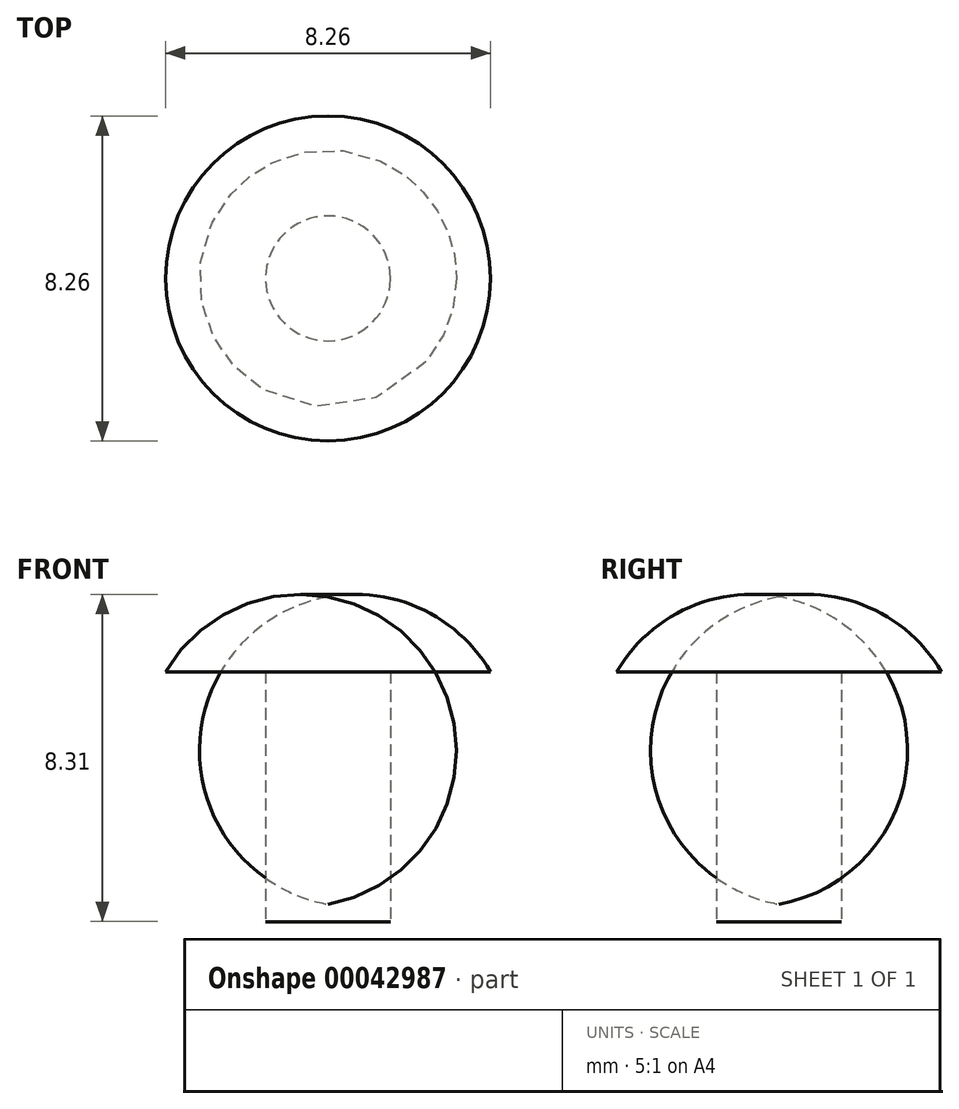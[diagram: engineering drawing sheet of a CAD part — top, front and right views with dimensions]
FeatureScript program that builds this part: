
annotation { "Feature Type Name" : "Feature", "Feature Type Description" : "" }
export const myFeature = defineFeature(function(context is Context, id is Id, definition is map)
    precondition{}
    {
        {
            var Q0;
            Q0=qCreatedBy(makeId("Front.planeOp"),FACE);
            var sketch = newSketch(context, id + "F0", { "sketchPlane" : qUnion([Q0])});
            skLineSegment(sketch, "E0", {"start": v(-16.44, 17.64) * mm, "end": v(-14.85, 17.64) * mm});
            skLineSegment(sketch, "E1", {"start": v(-14.85, 17.64) * mm, "end": v(-14.85, 23.99) * mm});
            skLineSegment(sketch, "E2", {"start": v(-16.44, 17.64) * mm, "end": v(-16.44, 25.9) * mm});
            skLineSegment(sketch, "E3", {"start": v(-14.85, 23.99) * mm, "end": v(-12.31, 23.99) * mm});
            skArc(sketch, "E4", {"start": v(-12.31, 23.99) * mm, "mid": v(-14.07, 25.59) * mm, "end": v(-16.44, 25.9) * mm});
            skSolve(sketch);
        }
        {
            var Q0;
            Q0=makeQuery(id+"F0.imprint","IMPRINT",FACE,{"disambiguationData":[TD([[makeQuery(id+"F0.imprint","IMPRINT",EDGE,{"derivedFrom":sQuery(id+"F0.wireOp",EDGE,"E0")}),1.0]])]});
            var Q1;
            Q1=sQuery(id+"F0.wireOp",EDGE,"E2");
            revolve(context, id + "F1", {"entities" : qUnion([Q0]), "axis" : qUnion([Q1]), "revolveType" : RevolveType.FULL});
        }
    });
